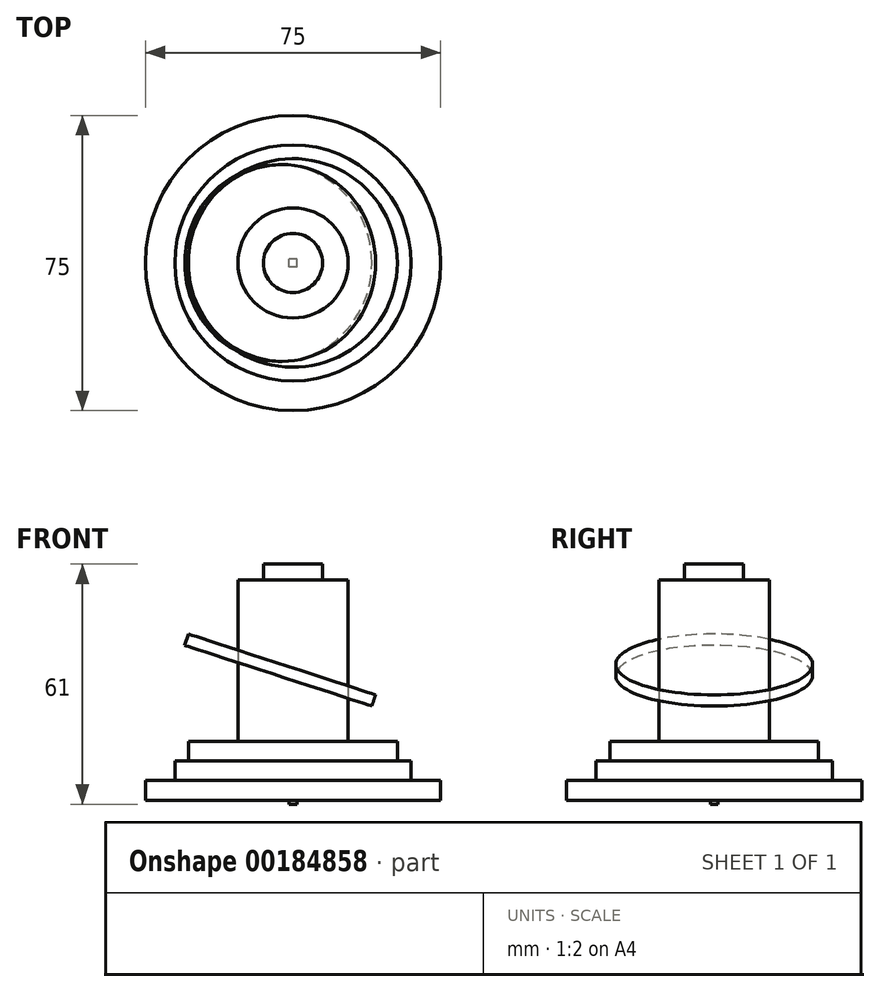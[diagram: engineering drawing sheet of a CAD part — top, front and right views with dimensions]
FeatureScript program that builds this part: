
annotation { "Feature Type Name" : "Feature", "Feature Type Description" : "" }
export const myFeature = defineFeature(function(context is Context, id is Id, definition is map)
    precondition{}
    {
        {
            var Q0;
            Q0=qCreatedBy(makeId("Front.planeOp"),FACE);
            var sketch = newSketch(context, id + "F0", { "sketchPlane" : qUnion([Q0])});
            skLineSegment(sketch, "E0.bottom", {"start": v(1, -1) * mm, "end": v(-1, -1) * mm});
            skLineSegment(sketch, "E0.top", {"start": v(1, 1) * mm, "end": v(-1, 1) * mm});
            skLineSegment(sketch, "E0.left", {"start": v(1, -1) * mm, "end": v(1, 1) * mm});
            skLineSegment(sketch, "E0.right", {"start": v(-1, -1) * mm, "end": v(-1, 1) * mm});
            skPoint(sketch, "E0.middle", {"position": v(0, 0) * mm});
            skSolve(sketch);
        }
        {
            var Q0;
            Q0 = qSketchRegion(id + "F0", true);
            extrude(context, id + "F1", {"entities" : qUnion([Q0]), "endBound" : BoundingType.SYMMETRIC, "depth" : 2 * mm});
        }
        {
            var Q0;
            Q0=qCreatedBy(makeId("Top.planeOp"),FACE);
            var sketch = newSketch(context, id + "F2", { "sketchPlane" : qUnion([Q0])});
            skCircle(sketch, "E1", {"center": v(0, 0) * mm, "radius": 7.5 * mm});
            skSolve(sketch);
        }
        {
            var Q0;
            Q0 = qSketchRegion(id + "F2", true);
            extrude(context, id + "F3", {"entities" : qUnion([Q0]), "depth" : 60 * mm});
        }
        {
            var Q0;
            Q0=qCreatedBy(makeId("Top.planeOp"),FACE);
            var sketch = newSketch(context, id + "F4", { "sketchPlane" : qUnion([Q0])});
            skCircle(sketch, "E2", {"center": v(0, 0) * mm, "radius": 14 * mm});
            skSolve(sketch);
        }
        {
            var Q0;
            Q0 = qSketchRegion(id + "F4", true);
            extrude(context, id + "F5", {"entities" : qUnion([Q0]), "operationType" : NewBodyOperationType.ADD, "depth" : 56 * mm});
        }
        {
            var Q0;
            Q0=qCreatedBy(makeId("Top.planeOp"),FACE);
            var sketch = newSketch(context, id + "F6", { "sketchPlane" : qUnion([Q0])});
            skCircle(sketch, "E3", {"center": v(0, 0) * mm, "radius": 37.5 * mm});
            skSolve(sketch);
        }
        {
            var Q0;
            Q0 = qSketchRegion(id + "F6", true);
            extrude(context, id + "F7", {"entities" : qUnion([Q0]), "operationType" : NewBodyOperationType.ADD, "depth" : 5 * mm});
        }
        {
            var Q0;
            Q0=qCreatedBy(makeId("Top.planeOp"),FACE);
            var sketch = newSketch(context, id + "F8", { "sketchPlane" : qUnion([Q0])});
            skCircle(sketch, "E4", {"center": v(0, 0) * mm, "radius": 30 * mm});
            skSolve(sketch);
        }
        {
            var Q0;
            Q0 = qSketchRegion(id + "F8", true);
            extrude(context, id + "F9", {"entities" : qUnion([Q0]), "operationType" : NewBodyOperationType.ADD, "depth" : 10 * mm});
        }
        {
            var Q0;
            Q0=qCreatedBy(makeId("Top.planeOp"),FACE);
            var sketch = newSketch(context, id + "F10", { "sketchPlane" : qUnion([Q0])});
            skCircle(sketch, "E5", {"center": v(0, 0) * mm, "radius": 26.5 * mm});
            skSolve(sketch);
        }
        {
            var Q0;
            Q0 = qSketchRegion(id + "F10", true);
            extrude(context, id + "F11", {"entities" : qUnion([Q0]), "operationType" : NewBodyOperationType.ADD, "depth" : 15 * mm});
        }
        {
            var Q0;
            Q0=qCreatedBy(makeId("Top.planeOp"),FACE);
            var sketch = newSketch(context, id + "F12", { "sketchPlane" : qUnion([Q0])});
            skCircle(sketch, "E6", {"center": v(0, 0) * mm, "radius": 25 * mm});
            skSolve(sketch);
        }
        {
            var Q0;
            Q0 = qSketchRegion(id + "F12", true);
            extrude(context, id + "F13", {"entities" : qUnion([Q0]), "depth" : 3 * mm});
        }
        {
            var Q0;
            Q0=makeQuery(id+"F13.opExtrude","SWEPT_BODY",BODY,{"disambiguationData":[OSD([sQuery(id+"F12.wireOp",EDGE,"E6")])]});
            var Q1;
            Q1=makeQuery(id+"F1.opExtrude","SWEPT_EDGE",EDGE,{"disambiguationData":[OSD([sQuery(id+"F0.wireOp",EDGE,"E0.bottom"),sQuery(id+"F0.wireOp",EDGE,"E0.right")])]});
            transform(context, id + "F14", {"entities" : qUnion([Q0]), "transformType" : TransformType.ROTATION, "transformAxis" : qUnion([Q1]), "angle" : 18 * degree, "makeCopy" : false});
        }
        {
            var Q0;
            Q0=makeQuery(id+"F13.opExtrude","SWEPT_BODY",BODY,{"disambiguationData":[OSD([sQuery(id+"F12.wireOp",EDGE,"E6")])]});
            transform(context, id + "F15", {"entities" : qUnion([Q0]), "transformType" : TransformType.TRANSLATION_3D, "dx" : -4 * mm, "dy" : 0 * mm, "dz" : 32 * mm, "makeCopy" : false});
        }
    });
